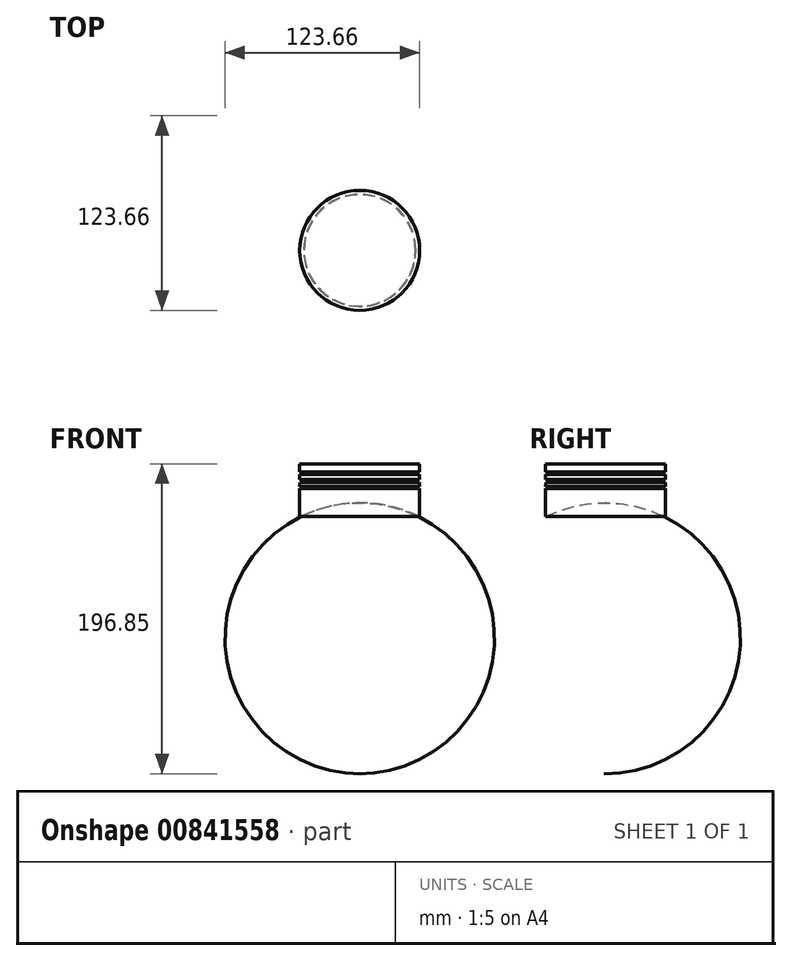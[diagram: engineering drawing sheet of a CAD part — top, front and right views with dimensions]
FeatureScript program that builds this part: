
annotation { "Feature Type Name" : "Feature", "Feature Type Description" : "" }
export const myFeature = defineFeature(function(context is Context, id is Id, definition is map)
    precondition{}
    {
        {
            var Q0;
            Q0=qCreatedBy(makeId("Front.planeOp"),FACE);
            var sketch = newSketch(context, id + "F0", { "sketchPlane" : qUnion([Q0])});
            skLineSegment(sketch, "E0", {"start": v(83.36, 0) * mm, "end": v(83.36, -5.08) * mm});
            skLineSegment(sketch, "E1", {"start": v(83.36, -6.73) * mm, "end": v(83.36, -9.86) * mm});
            skLineSegment(sketch, "E2", {"start": v(83.36, -9.86) * mm, "end": v(80.8, -9.86) * mm});
            skLineSegment(sketch, "E3", {"start": v(80.8, -9.86) * mm, "end": v(80.8, -11.7) * mm});
            skLineSegment(sketch, "E4", {"start": v(80.8, -11.7) * mm, "end": v(83.2, -11.7) * mm});
            skLineSegment(sketch, "E5", {"start": v(83.2, -11.7) * mm, "end": v(83.36, -14.29) * mm});
            skLineSegment(sketch, "E6", {"start": v(83.36, -14.29) * mm, "end": v(80.82, -14.44) * mm});
            skLineSegment(sketch, "E7", {"start": v(80.82, -14.44) * mm, "end": v(80.9, -15.7) * mm});
            skLineSegment(sketch, "E8", {"start": v(80.9, -15.7) * mm, "end": v(83.36, -15.7) * mm});
            skLineSegment(sketch, "E9", {"start": v(83.36, -15.7) * mm, "end": v(83.36, -33.46) * mm});
            skLineSegment(sketch, "E10", {"start": v(83.36, 0) * mm, "end": v(45.26, 0) * mm});
            skLineSegment(sketch, "E11", {"start": v(45.26, 0) * mm, "end": v(45.26, -24.8) * mm});
            skArc(sketch, "E12", {"start": v(83.36, -33.46) * mm, "mid": v(64.8, -26.94) * mm, "end": v(45.26, -24.8) * mm});
            skLineSegment(sketch, "E13", {"start": v(83.36, -5.08) * mm, "end": v(80.64, -5.08) * mm});
            skLineSegment(sketch, "E14", {"start": v(80.64, -5.08) * mm, "end": v(80.64, -6.73) * mm});
            skLineSegment(sketch, "E15", {"start": v(80.64, -6.73) * mm, "end": v(83.36, -6.73) * mm});
            skSolve(sketch);
        }
        {
            var Q0;
            Q0=makeQuery(id+"F0.imprint","IMPRINT",FACE,{"disambiguationData":[TD([[makeQuery(id+"F0.imprint","IMPRINT",EDGE,{"derivedFrom":sQuery(id+"F0.wireOp",EDGE,"E0")}),-1.0]])]});
            var Q1;
            Q1=sQuery(id+"F0.wireOp",EDGE,"E11");
            revolve(context, id + "F1", {"surfaceOperationType" : NewSurfaceOperationType.NEW, "entities" : qUnion([Q0]), "axis" : qUnion([Q1]), "revolveType" : RevolveType.FULL});
        }
    });
